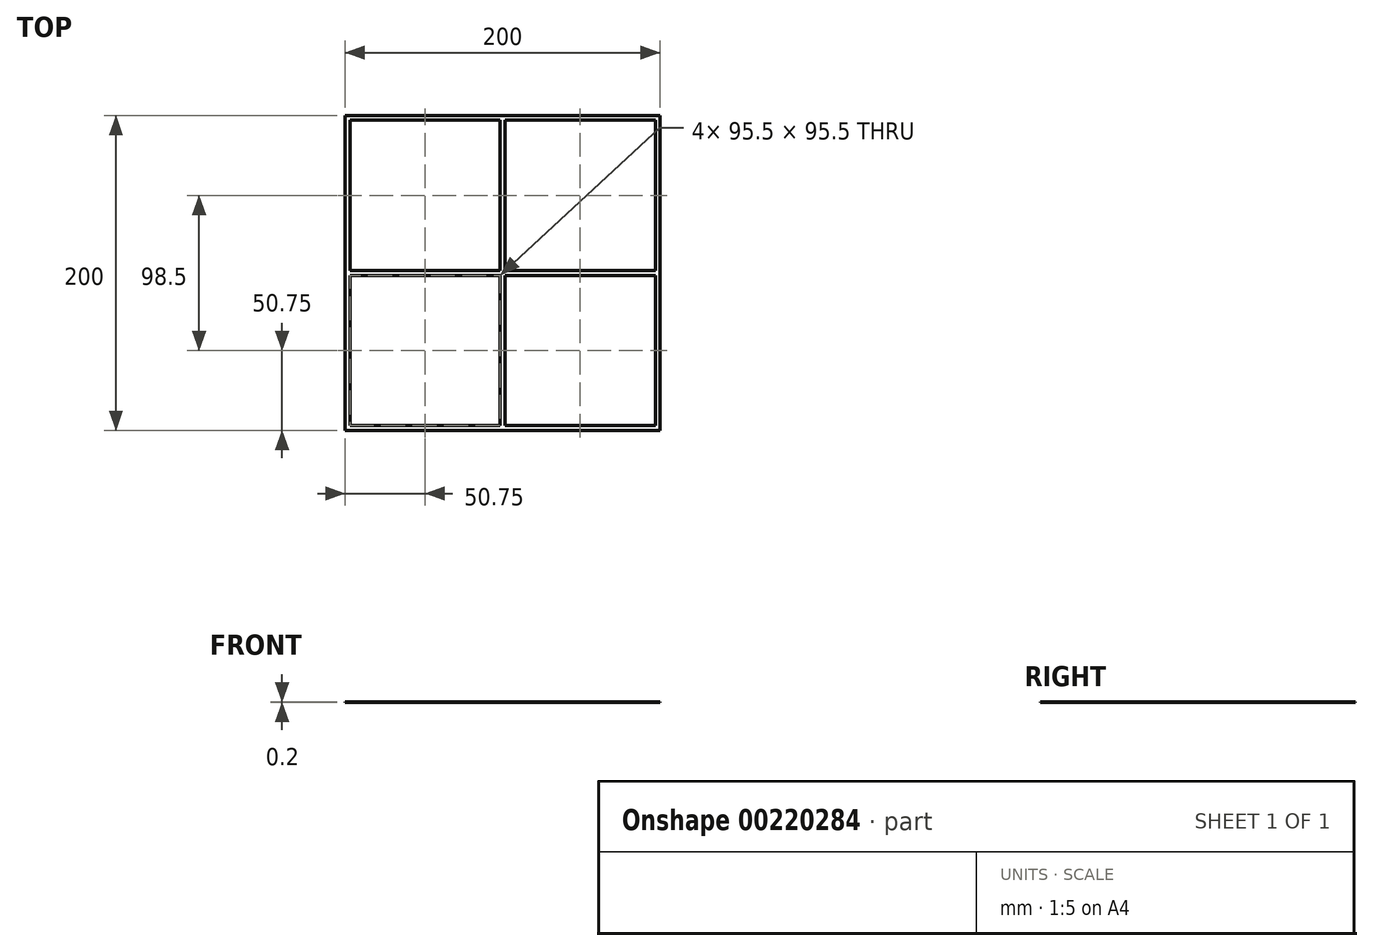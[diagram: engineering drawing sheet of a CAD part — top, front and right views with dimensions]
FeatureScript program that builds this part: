
annotation { "Feature Type Name" : "Feature", "Feature Type Description" : "" }
export const myFeature = defineFeature(function(context is Context, id is Id, definition is map)
    precondition{}
    {
        {
            var Q0;
            Q0=qCreatedBy(makeId("Top.planeOp"),FACE);
            var sketch = newSketch(context, id + "F0", { "sketchPlane" : qUnion([Q0])});
            skLineSegment(sketch, "E0.bottom", {"start": v(100, -100) * mm, "end": v(-100, -100) * mm});
            skLineSegment(sketch, "E0.top", {"start": v(100, 100) * mm, "end": v(-100, 100) * mm});
            skLineSegment(sketch, "E0.left", {"start": v(100, -100) * mm, "end": v(100, 100) * mm});
            skLineSegment(sketch, "E0.right", {"start": v(-100, -100) * mm, "end": v(-100, 100) * mm});
            skPoint(sketch, "E0.middle", {"position": v(0, 0) * mm});
            skLineSegment(sketch, "E1.bottom", {"start": v(97, 97) * mm, "end": v(1.5, 97) * mm});
            skLineSegment(sketch, "E1.top", {"start": v(97, -97) * mm, "end": v(1.5, -97) * mm});
            skLineSegment(sketch, "E1.left", {"start": v(97, 97) * mm, "end": v(97, 1.5) * mm});
            skLineSegment(sketch, "E1.right", {"start": v(-97, 97) * mm, "end": v(-97, 1.5) * mm});
            skLineSegment(sketch, "E2.bottom", {"start": v(97, -1.5) * mm, "end": v(1.5, -1.5) * mm});
            skLineSegment(sketch, "E2.top", {"start": v(97, 1.5) * mm, "end": v(1.5, 1.5) * mm});
            skLineSegment(sketch, "E2.left", {"start": v(100, -1.5) * mm, "end": v(100, 1.5) * mm});
            skLineSegment(sketch, "E2.right", {"start": v(-100, -1.5) * mm, "end": v(-100, 1.5) * mm});
            skLineSegment(sketch, "E3.bottom", {"start": v(1.5, 100) * mm, "end": v(-1.5, 100) * mm});
            skLineSegment(sketch, "E3.top", {"start": v(1.5, -100) * mm, "end": v(-1.5, -100) * mm});
            skLineSegment(sketch, "E3.left", {"start": v(1.5, 97) * mm, "end": v(1.5, 1.5) * mm});
            skLineSegment(sketch, "E3.right", {"start": v(-1.5, 97) * mm, "end": v(-1.5, 1.5) * mm});
            skLineSegment(sketch, "E4.trimOffspring", {"start": v(-1.5, 97) * mm, "end": v(-97, 97) * mm});
            skLineSegment(sketch, "E5.trimOffspring", {"start": v(1.5, -1.5) * mm, "end": v(1.5, -97) * mm});
            skLineSegment(sketch, "E6.trimOffspring", {"start": v(-1.5, 1.5) * mm, "end": v(-97, 1.5) * mm});
            skLineSegment(sketch, "E7.trimOffspring", {"start": v(-1.5, -1.5) * mm, "end": v(-1.5, -97) * mm});
            skLineSegment(sketch, "E8.trimOffspring", {"start": v(-1.5, -1.5) * mm, "end": v(-97, -1.5) * mm});
            skLineSegment(sketch, "E9.trimOffspring", {"start": v(97, -1.5) * mm, "end": v(97, -97) * mm});
            skLineSegment(sketch, "E10.trimOffspring", {"start": v(-97, -1.5) * mm, "end": v(-97, -97) * mm});
            skLineSegment(sketch, "E11.trimOffspring", {"start": v(-1.5, -97) * mm, "end": v(-97, -97) * mm});
            skSolve(sketch);
        }
        {
            var Q0;
            Q0 = qSketchRegion(id + "F0", true);
            extrude(context, id + "F1", {"entities" : qUnion([Q0]), "depth" : 0.2 * mm});
        }
    });
